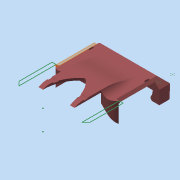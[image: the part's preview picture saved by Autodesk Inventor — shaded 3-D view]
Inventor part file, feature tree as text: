
AUTODESK INVENTOR PART (.ipt)
format: ipt  version: 2015 SP1 (Build 190203100, 203)  size: 1,085,440 bytes
history: native  units: in
note: dims shown in document units (in); Inventor stores cm internally (conversion verified against a paired STEP export)
features: projected_geometry x34, fillet x31, sketch x30, extrude x28, chamfer x16, move_body x4, plane x2, direct_edit x2
ambient origin geometry x8: Origin, YZ Plane, XZ Plane, XY Plane, X Axis, Y Axis, Z Axis, Center Point
bodies: Solid1 (feature_tree), Solid2 (feature_tree)
feature tree (147):
  extrude  "Extrusion1"  Depth=0.22in
  plane  "Work Plane1"
  extrude  "Extrusion2"  Depth=5.097in
  chamfer  "Chamfer1"  Distance=0.25in
  chamfer  "Chamfer2"  Distance=0.25in
  chamfer  "Chamfer3"  Distance=0.125in Angle=45.0deg
  chamfer  "Chamfer4"  Distance=0.125in Angle=45.0deg
  chamfer  "Chamfer5"  Distance=0.125in Angle=45.0deg
  fillet  "Fillet1"  Radius=2.0in
  extrude  "Extrusion3"  Depth=0.25in
  extrude  "Extrusion4"  Depth=0.125in
  extrude  "Extrusion5"  Depth=0.5512in
  extrude  "Extrusion6"  Depth=0.25in
  chamfer  "Chamfer6"  Distance=0.25in
  chamfer  "Chamfer7"  Distance=1.25in
  fillet  "Fillet2"  Radius=0.0787in
  extrude  "Extrusion7"  Depth=0.125in TaperAngle=45.0deg
  chamfer  "Chamfer8"  Distance=0.125in Angle=45.0deg
  fillet  "Fillet3"  Radius=0.125in
  extrude  "Extrusion8"  Depth=0.0394in
  fillet  "Fillet4"  Radius=0.0295in
  fillet  "Fillet5"  Radius=0.25in
  chamfer  "Chamfer9"  Distance=0.375in
  extrude  "Extrusion9"  Depth=0.125in
  sketch  "Sketch10"  dims[d11=0.375in]
  extrude  "Extrusion10"  Depth=0.125in TaperAngle=0.0deg
  fillet  "Fillet7"  Radius=0.5in
  plane  "Work Plane2"
  sketch  "Sketch12"  dims[d15=-1.5157in]
  extrude  "Extrusion11"  Depth=0.125in
  extrude  "Extrusion12"  Depth=0.125in TaperAngle=45.0deg
  extrude  "Extrusion13"  Depth=0.125in TaperAngle=0.0deg
  extrude  "Extrusion14"  Depth=0.125in
  fillet  "Fillet8"  Radius=0.125in
  fillet  "Fillet9"  Radius=1.0in
  fillet  "Fillet10"  Radius=0.125in
  fillet  "Fillet11"  Radius=0.125in
  chamfer  "Chamfer10"  Distance=0.25in
  fillet  "Fillet12"  Radius=0.125in
  extrude  "Extrusion15"  Depth=0.125in
  fillet  "Fillet13"  Radius=0.125in
  extrude  "Extrusion16"  Depth=0.125in
  extrude  "Extrusion17"  Depth=0.125in TaperAngle=0.0deg
  extrude  "Extrusion18"  Depth=0.125in
  fillet  "Fillet14"  Radius=3.0in
  chamfer  "Chamfer11"  Distance=0.5in
  chamfer  "Chamfer12"  Distance=0.5in
  chamfer  "Chamfer13"  Distance=0.125in Angle=45.0deg
  extrude  "Extrusion19"  Depth=0.125in
  extrude  "Extrusion20"  Depth=0.125in TaperAngle=0.0deg
  extrude  "Extrusion21"  Depth=0.125in
  extrude  "Extrusion22"  Depth=0.125in
  extrude  "Extrusion23"  Depth=0.125in
  extrude  "Extrusion24"  Depth=0.125in TaperAngle=0.0deg
  extrude  "Extrusion25"  Depth=0.125in TaperAngle=0.0deg
  fillet  "Fillet17"  Radius=0.5in
  extrude  "Extrusion26"  Depth=0.125in
  fillet  "Fillet18"  Radius=0.125in
  fillet  "Fillet19"  Radius=0.125in
  fillet  "Fillet20"  Radius=0.125in
  fillet  "Fillet21"  Radius=0.0394in
  chamfer  "Chamfer14"  Distance=0.0394in
  fillet  "Fillet22"  Radius=0.0394in
  direct_edit  "Direct Edit1"
  direct_edit  "Direct Edit2"
  extrude  "Extrusion27"  Depth=0.125in
  fillet  "Fillet23"  Radius=0.25in
  fillet  "Fillet24"  Radius=0.25in
  fillet  "Fillet25"  Radius=0.0938in
  fillet  "Fillet26"  Radius=0.125in
  fillet  "Fillet27"  Radius=0.375in
  chamfer  "Chamfer15"  Distance=0.25in
  fillet  "Fillet28"  Radius=0.0938in
  fillet  "Fillet29"  Radius=0.0938in
  fillet  "Fillet30"  Radius=0.25in
  fillet  "Fillet31"  Radius=0.25in
  fillet  "Fillet32"  Radius=0.0938in
  fillet  "Fillet33"  Radius=0.25in
  fillet  "Fillet34"  Radius=0.0938in
  extrude  "Extrusion28"  Depth=0.125in
  chamfer  "Chamfer16"  Distance=0.375in
  sketch  "Sketch1"  dims[d0=0.22in d1=0.22in]
  sketch  "Sketch2"  dims[d2=0.22in d3=5.097in]
  projected_geometry  "Projected Loop1"
  sketch  "Sketch3"  dims[d4=5.097in]
  projected_geometry  "Projected Loop2"
  sketch  "Sketch4"  dims[d5=3.187in]
  sketch  "Sketch5"  dims[d6=1.496in]
  sketch  "Sketch6"  dims[d7=2.217in]
  projected_geometry  "Projected Loop3"
  projected_geometry  "Projected Loop4"
  sketch  "Sketch7"  dims[d8=0.25in]
  projected_geometry  "Projected Loop5"
  sketch  "Sketch8"  dims[d9=0.375in]
  projected_geometry  "Projected Loop6"
  sketch  "Sketch9"  dims[d10=0.375in]
  projected_geometry  "Projected Loop7"
  projected_geometry  "Projected Loop8"
  projected_geometry  "Projected Loop9"
  projected_geometry  "Projected Loop10"
  sketch  "Sketch11"  dims[d12=0.375in d13=0.25in d14=0.0in]
  projected_geometry  "Projected Loop11"
  projected_geometry  "Projected Loop12"
  sketch  "Sketch13"  dims[d16=0.25in]
  sketch  "Sketch14"  dims[d17=0.25in d18=0.25in d19=0.0in d20=0.75in d21=0.125in d22=45.0deg d23=1.0in d24=0.125in d25=45.0deg d26=0.5in d27=0.125in d28=45.0deg]
  projected_geometry  "Projected Loop13"
  projected_geometry  "Projected Loop14"
  sketch  "Sketch15"  dims[d29=0.25in d30=0.125in d31=45.0deg]
  sketch  "Sketch16"  dims[d32=0.5in d33=0.125in d34=45.0deg d35=2.0in]
  projected_geometry  "Projected Loop15"
  sketch  "Sketch17"  dims[d36=0.0938in d37=0.25in]
  projected_geometry  "Projected Loop16"
  projected_geometry  "Projected Loop17"
  projected_geometry  "Projected Loop18"
  sketch  "Sketch19"  dims[d38=0.5in d39=0.125in]
  projected_geometry  "Projected Loop20"
  sketch  "Sketch20"  dims[d40=0.25in d41=0.0in d42=0.5512in]
  projected_geometry  "Projected Loop21"
  sketch  "Sketch21"  dims[d43=0.7087in d44=0.25in]
  projected_geometry  "Projected Loop22"
  sketch  "Sketch22"  dims[d45=0.5in d46=0.25in d47=0.0in]
  projected_geometry  "Projected Loop23"
  projected_geometry  "Projected Loop24"
  sketch  "Sketch23"  dims[d48=0.0394in]
  projected_geometry  "Projected Loop25"
  sketch  "Sketch24"  dims[d49=0.4921in]
  sketch  "Sketch25"  dims[d50=0.0591in]
  projected_geometry  "Projected Loop26"
  projected_geometry  "Projected Loop27"
  sketch  "Sketch26"  dims[d51=0.2362in d52=1.25in d53=0.0in d54=0.0787in]
  sketch  "Sketch27"  dims[d55=1.25in d56=0.0in d57=0.125in d58=0.125in d59=45.0deg d60=0.2188in d61=0.125in d62=45.0deg d63=0.125in]
  projected_geometry  "Projected Loop28"
  projected_geometry  "Projected Loop29"
  sketch  "Sketch28"  dims[d64=0.0394in d65=0.0394in d66=0.0295in d67=0.0in]
  projected_geometry  "Projected Loop30"
  projected_geometry  "Projected Loop31"
  sketch  "Sketch29"  dims[d68=0.0295in d69=0.125in d70=45.0deg d71=0.25in]
  projected_geometry  "Projected Loop32"
  projected_geometry  "Projected Loop33"
  sketch  "Sketch30"  dims[d72=0.375in]
  projected_geometry  "Projected Loop34"
  projected_geometry  "Projected Loop35"
  sketch  "Sketch31"  dims[d73=2.0in d74=0.375in d75=2.0in d76=1.0in d77=0.0in d78=0.5in d79=0.125in d80=0.25in d81=0.125in d82=45.0deg d83=0.125in d84=0.0in d85=0.125in d86=0.125in d87=0.0in d89=1.0in d90=0.125in d91=0.125in d92=0.0in d93=0.25in d94=0.125in d95=0.0in d96=0.25in d97=0.125in d98=0.0in d99=0.5in d100=0.125in d101=0.0in d102=3.0in d103=3.0in d104=0.5in d105=0.5in d106=0.125in d107=0.125in d108=45.0deg d109=0.125in d110=0.125in d111=0.0in d112=0.25in d115=0.1875in d116=0.1875in d117=0.125in d118=0.0in d119=0.5in d120=0.0in d121=0.5in d122=0.0in d123=0.25in d125=0.25in d126=0.125in d127=45.0deg d128=0.0625in d129=0.125in d130=45.0deg d131=0.5in d132=0.125in d133=45.0deg d135=0.0394in d136=0.0394in d137=0.0394in d138=0.0in d139=0.5in d140=0.25in d141=0.0in d142=0.25in d143=0.0938in d144=0.125in d145=0.375in d146=0.25in d147=0.0in d148=0.0938in d149=0.0938in d150=0.25in d151=0.0in d152=0.25in d153=0.0938in d154=0.25in d155=0.0938in d156=0.125in d157=0.375in d158=0.375in d159=0.25in d160=0.0in d161=0.0938in d162=0.0938in d163=0.25in d164=0.0in d165=0.0625in d166=0.0in d167=0.125in d168=0.0625in d169=0.0in d170=5.0in d171=5.0in d172=0.5in d173=0.5in d174=0.375in d175=0.125in d176=45.0deg d177=0.125in d178=0.0in d179=0.0in d180=-0.0079in d181=0.0in d182=0.0in d183=-0.0079in d184=0.0in d185=0.0in d186=-0.0079in d187=0.0in d188=0.0in d189=-0.0079in d190=0.0197in d191=0.0in d192=0.0625in d193=0.25in d194=0.125in d195=0.5in d196=0.5in d197=0.7087in d198=0.125in d199=45.0deg d200=2.0in d201=0.125in d202=0.0625in d203=0.5in d204=0.125in d205=0.125in d206=0.125in d207=0.0394in d208=0.0in d209=0.0394in d210=0.125in d211=45.0deg]
  move_body  "Move1"
  move_body  "Move2"
  move_body  "Move3"
  move_body  "Move4"
